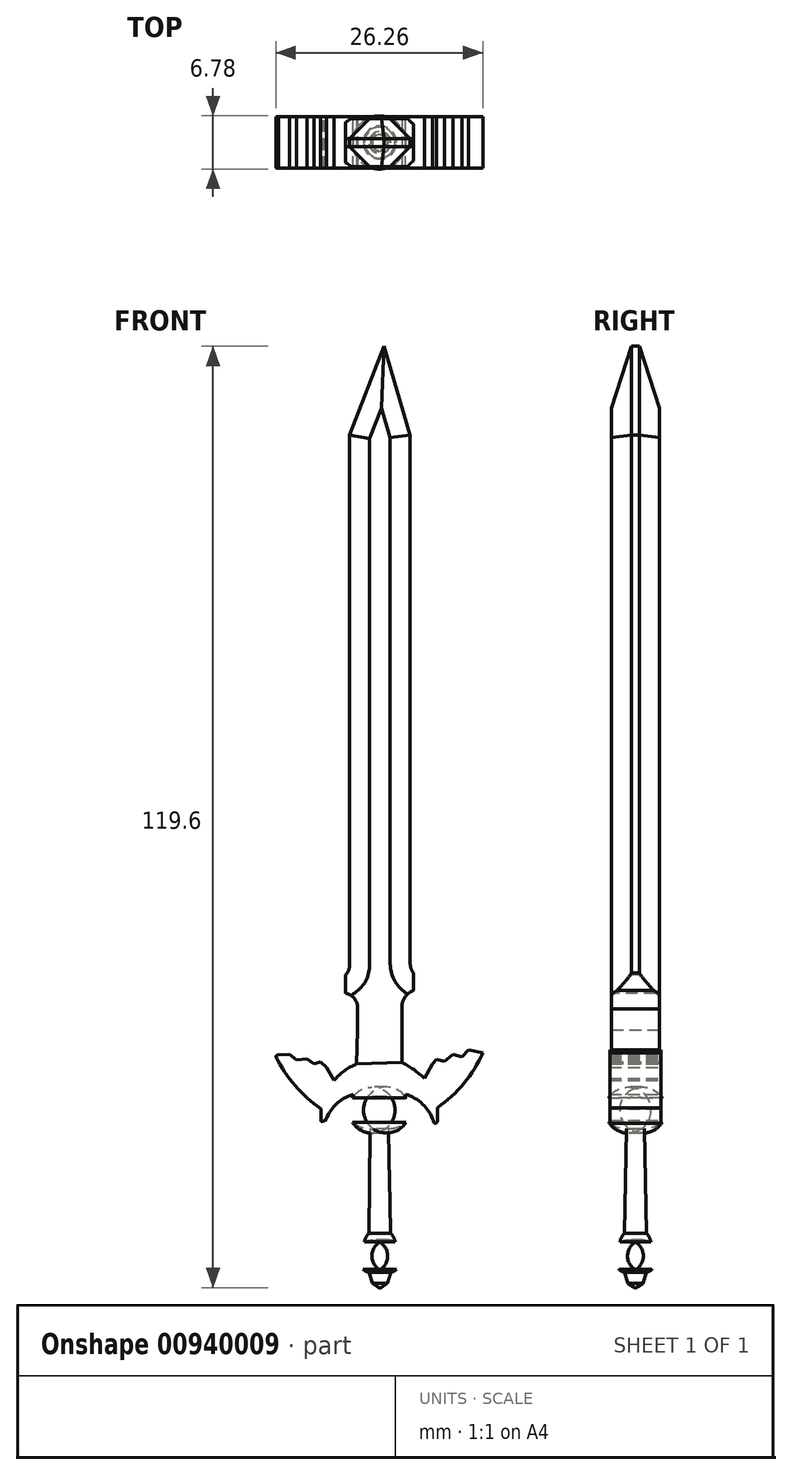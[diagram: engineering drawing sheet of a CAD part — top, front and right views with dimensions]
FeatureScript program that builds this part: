
annotation { "Feature Type Name" : "Feature", "Feature Type Description" : "" }
export const myFeature = defineFeature(function(context is Context, id is Id, definition is map)
    precondition{}
    {
        {
            var Q0;
            Q0=qCreatedBy(makeId("Front.planeOp"),FACE);
            var sketch = newSketch(context, id + "F0", { "sketchPlane" : qUnion([Q0])});
            skLineSegment(sketch, "E0", {"start": v(-4.41, -18.46) * mm, "end": v(-4.41, 49) * mm});
            skLineSegment(sketch, "E1", {"start": v(-4.41, 49) * mm, "end": v(0, 60.26) * mm});
            skLineSegment(sketch, "E2", {"start": v(0, 60.26) * mm, "end": v(3.3, 49) * mm});
            skLineSegment(sketch, "E3", {"start": v(3.3, 49) * mm, "end": v(3.3, -18.19) * mm});
            skArc(sketch, "E4", {"start": v(3.3, -18.19) * mm, "mid": v(3.41, -18.8) * mm, "end": v(3.72, -19.36) * mm});
            skLineSegment(sketch, "E5", {"start": v(3.72, -19.36) * mm, "end": v(3.72, -21.6) * mm});
            skArc(sketch, "E6", {"start": v(3.72, -21.6) * mm, "mid": v(2.57, -22.5) * mm, "end": v(2.26, -23.94) * mm});
            skArc(sketch, "E7", {"start": v(-4.9, -19.6) * mm, "mid": v(-4.54, -19.08) * mm, "end": v(-4.41, -18.46) * mm});
            skLineSegment(sketch, "E8", {"start": v(-4.9, -19.6) * mm, "end": v(-4.9, -21.94) * mm});
            skArc(sketch, "E9", {"start": v(-3.4, -23.94) * mm, "mid": v(-3.74, -22.63) * mm, "end": v(-4.9, -21.94) * mm});
            skLineSegment(sketch, "E10", {"start": v(-3.4, -23.94) * mm, "end": v(-3.4, -26.65) * mm});
            skLineSegment(sketch, "E11", {"start": v(2.26, -23.94) * mm, "end": v(2.26, -26.72) * mm});
            skLineSegment(sketch, "E12", {"start": v(2.26, -26.72) * mm, "end": v(2.28, -30.73) * mm});
            skArc(sketch, "E13", {"start": v(5.1, -32.73) * mm, "mid": v(3.76, -31.63) * mm, "end": v(2.28, -30.73) * mm});
            skLineSegment(sketch, "E14", {"start": v(5.1, -32.73) * mm, "end": v(6.16, -30.9) * mm});
            skLineSegment(sketch, "E15", {"start": v(6.16, -30.9) * mm, "end": v(6.67, -30.32) * mm});
            skLineSegment(sketch, "E16", {"start": v(6.67, -30.32) * mm, "end": v(7.65, -30.56) * mm});
            skLineSegment(sketch, "E17", {"start": v(7.65, -30.56) * mm, "end": v(8.74, -29.67) * mm});
            skLineSegment(sketch, "E18", {"start": v(8.74, -29.67) * mm, "end": v(9.9, -30.02) * mm});
            skLineSegment(sketch, "E19", {"start": v(9.9, -30.02) * mm, "end": v(10.74, -29.1) * mm});
            skLineSegment(sketch, "E20", {"start": v(10.74, -29.1) * mm, "end": v(12.53, -29.5) * mm});
            skArc(sketch, "E21", {"start": v(6.77, -36.46) * mm, "mid": v(10.13, -33.38) * mm, "end": v(12.53, -29.5) * mm});
            skLineSegment(sketch, "E22", {"start": v(6.77, -36.46) * mm, "end": v(6.77, -38.17) * mm});
            skArc(sketch, "E23", {"start": v(6.25, -38.17) * mm, "mid": v(6.51, -38.43) * mm, "end": v(6.77, -38.17) * mm});
            skArc(sketch, "E24", {"start": v(-8.05, -38.05) * mm, "mid": v(-7.96, -38.22) * mm, "end": v(-7.78, -38.17) * mm});
            skLineSegment(sketch, "E25", {"start": v(-8.05, -38.05) * mm, "end": v(-8.05, -36.59) * mm});
            skArc(sketch, "E26", {"start": v(-13.73, -30) * mm, "mid": v(-11.32, -33.67) * mm, "end": v(-8.05, -36.59) * mm});
            skArc(sketch, "E27", {"start": v(-13.45, -29.79) * mm, "mid": v(-13.64, -29.83) * mm, "end": v(-13.73, -30) * mm});
            skLineSegment(sketch, "E28", {"start": v(-13.45, -29.79) * mm, "end": v(-12.03, -29.7) * mm});
            skLineSegment(sketch, "E29", {"start": v(-12.03, -29.7) * mm, "end": v(-11.11, -30.37) * mm});
            skLineSegment(sketch, "E30", {"start": v(-11.11, -30.37) * mm, "end": v(-9.82, -30.24) * mm});
            skLineSegment(sketch, "E31", {"start": v(-9.82, -30.24) * mm, "end": v(-8.94, -30.88) * mm});
            skLineSegment(sketch, "E32", {"start": v(-8.94, -30.88) * mm, "end": v(-8.08, -30.65) * mm});
            skLineSegment(sketch, "E33", {"start": v(-8.08, -30.65) * mm, "end": v(-7.3, -31.32) * mm});
            skLineSegment(sketch, "E34", {"start": v(-7.3, -31.32) * mm, "end": v(-6.38, -33.01) * mm});
            skLineSegment(sketch, "E35", {"start": v(-3.4, -26.65) * mm, "end": v(-3.5, -30.93) * mm});
            skArc(sketch, "E36", {"start": v(-3.5, -30.93) * mm, "mid": v(-5.06, -31.8) * mm, "end": v(-6.38, -33.01) * mm});
            skArc(sketch, "E37", {"start": v(3.41, -37.88) * mm, "mid": v(3.4, -36.45) * mm, "end": v(2.7, -35.2) * mm});
            skArc(sketch, "E38", {"start": v(1.2, -39.14) * mm, "mid": v(2.34, -38.58) * mm, "end": v(3.41, -37.88) * mm});
            skArc(sketch, "E39", {"start": v(-4, -38.36) * mm, "mid": v(-2.95, -38.94) * mm, "end": v(-1.76, -39.14) * mm});
            skArc(sketch, "E40", {"start": v(-4, -35.2) * mm, "mid": v(-4.47, -36.78) * mm, "end": v(-4, -38.36) * mm});
            skLineSegment(sketch, "E41", {"start": v(-1.76, -39.14) * mm, "end": v(-1.95, -52.43) * mm});
            skLineSegment(sketch, "E42", {"start": v(1.2, -39.14) * mm, "end": v(1.2, -52.43) * mm});
            skArc(sketch, "E43", {"start": v(1.72, -53.51) * mm, "mid": v(1.63, -52.89) * mm, "end": v(1.2, -52.43) * mm});
            skArc(sketch, "E44", {"start": v(1.72, -57.03) * mm, "mid": v(2.81, -55.27) * mm, "end": v(1.72, -53.51) * mm});
            skArc(sketch, "E45", {"start": v(1.2, -57.15) * mm, "mid": v(1.46, -57.11) * mm, "end": v(1.72, -57.03) * mm});
            skArc(sketch, "E46", {"start": v(-2.52, -53.51) * mm, "mid": v(-3.6, -55.23) * mm, "end": v(-2.67, -57.03) * mm});
            skArc(sketch, "E47", {"start": v(-2.67, -57.03) * mm, "mid": v(-2.33, -57.25) * mm, "end": v(-1.95, -57.4) * mm});
            skLineSegment(sketch, "E48", {"start": v(-1.95, -57.4) * mm, "end": v(-1.5, -58.76) * mm});
            skLineSegment(sketch, "E49", {"start": v(-1.5, -58.76) * mm, "end": v(-0.82, -59.25) * mm});
            skArc(sketch, "E50", {"start": v(-0.82, -59.25) * mm, "mid": v(-0.54, -59.34) * mm, "end": v(-0.26, -59.25) * mm});
            skLineSegment(sketch, "E51", {"start": v(-0.26, -59.25) * mm, "end": v(0.55, -58.83) * mm});
            skLineSegment(sketch, "E52", {"start": v(0.55, -58.83) * mm, "end": v(1.2, -57.15) * mm});
            skArc(sketch, "E53", {"start": v(-1.95, -52.43) * mm, "mid": v(-2.31, -52.93) * mm, "end": v(-2.52, -53.51) * mm});
            skLineSegment(sketch, "E54", {"start": v(-0.63, -21.55) * mm, "end": v(-0.63, -21.55) * mm});
            skLineSegment(sketch, "E55", {"start": v(-1.95, -52.43) * mm, "end": v(1.2, -52.43) * mm});
            skPoint(sketch, "E56.0.midPoint", {"position": v(-0.63, -21.55) * mm});
            skLineSegment(sketch, "E57", {"start": v(-3.5, -30.93) * mm, "end": v(2.28, -30.73) * mm});
            skLineSegment(sketch, "E58", {"start": v(-0.63, -34.53) * mm, "end": v(-0.54, -58.87) * mm});
            skLineSegment(sketch, "E59", {"start": v(-0.54, -58.87) * mm, "end": v(-0.54, -59.34) * mm});
            skPoint(sketch, "E60.orphan", {"position": v(0.17, -34.5) * mm});
            skPoint(sketch, "E61.orphan", {"position": v(-1.43, -34.57) * mm});
            skLineSegment(sketch, "E62", {"start": v(2.7, -35.2) * mm, "end": v(2.7, -34.76) * mm});
            skLineSegment(sketch, "E63.MirrorCS", {"start": v(-3.95, -35.23) * mm, "end": v(-3.96, -34.79) * mm});
            skLineSegment(sketch, "E64", {"start": v(-3.95, -35.23) * mm, "end": v(-4, -35.2) * mm});
            skArc(sketch, "E65", {"start": v(6.25, -38.17) * mm, "mid": v(4.9, -36.03) * mm, "end": v(2.7, -34.76) * mm});
            skArc(sketch, "E66.MirrorCS", {"start": v(-7.48, -38.22) * mm, "mid": v(-6.14, -36.07) * mm, "end": v(-3.96, -34.79) * mm});
            skLineSegment(sketch, "E67", {"start": v(-7.48, -38.22) * mm, "end": v(-7.78, -38.17) * mm});
            skLineSegment(sketch, "E68", {"start": v(2.7, -35.2) * mm, "end": v(-3.95, -35.23) * mm});
            skSolve(sketch);
        }
        {
            var Q0;
            Q0=makeQuery(id+"F0.imprint","IMPRINT",FACE,{"disambiguationData":[TD([[makeQuery(id+"F0.imprint","IMPRINT",EDGE,{"derivedFrom":sQuery(id+"F0.wireOp",EDGE,"E39")}),1.0]])]});
            var Q1;
            Q1=makeQuery(id+"F0.imprint","IMPRINT",FACE,{"disambiguationData":[TD([[makeQuery(id+"F0.imprint","IMPRINT",EDGE,{"derivedFrom":sQuery(id+"F0.wireOp",EDGE,"E46")}),1.0]])]});
            var Q2;
            Q2=sQuery(id+"F0.wireOp",EDGE,"E58");
            revolve(context, id + "F1", {"surfaceOperationType" : NewSurfaceOperationType.NEW, "entities" : qUnion([Q0, Q1]), "axis" : qUnion([Q2]), "revolveType" : RevolveType.FULL});
        }
        {
            var Q0;
            Q0=makeQuery(id+"F0.imprint","IMPRINT",FACE,{"disambiguationData":[TD([[makeQuery(id+"F0.imprint","IMPRINT",EDGE,{"derivedFrom":sQuery(id+"F0.wireOp",EDGE,"E13")}),1.0]])]});
            extrude(context, id + "F2", {"entities" : qUnion([Q0]), "operationType" : NewBodyOperationType.ADD, "endBound" : BoundingType.SYMMETRIC, "depth" : 6.5 * mm, "offsetDistance" : 25.4 * mm});
        }
        {
            var Q0;
            Q0=makeQuery(id+"F0.imprint","IMPRINT",FACE,{"disambiguationData":[TD([[makeQuery(id+"F0.imprint","IMPRINT",EDGE,{"derivedFrom":sQuery(id+"F0.wireOp",EDGE,"E0")}),-1.0]])]});
            extrude(context, id + "F3", {"entities" : qUnion([Q0]), "operationType" : NewBodyOperationType.ADD, "endBound" : BoundingType.SYMMETRIC, "oppositeDirection" : true, "depth" : 6.1 * mm, "offsetDistance" : 25.4 * mm});
        }
        {
            var Q0;
            Q0=makeQuery(id+"F3.opExtrude","CAP_EDGE",EDGE,{"disambiguationData":[OSD([sQuery(id+"F0.wireOp",EDGE,"E1")])],"isStart":false});
            var Q1;
            Q1=makeQuery(id+"F3.opExtrude","CAP_EDGE",EDGE,{"disambiguationData":[OSD([sQuery(id+"F0.wireOp",EDGE,"E1")])],"isStart":true});
            var Q2;
            Q2=makeQuery(id+"F3.opExtrude","CAP_EDGE",EDGE,{"disambiguationData":[OSD([sQuery(id+"F0.wireOp",EDGE,"E0")])],"isStart":true});
            var Q3;
            Q3=makeQuery(id+"F3.opExtrude","CAP_EDGE",EDGE,{"disambiguationData":[OSD([sQuery(id+"F0.wireOp",EDGE,"E0")])],"isStart":false});
            var Q4;
            Q4=makeQuery(id+"F3.opExtrude","CAP_EDGE",EDGE,{"disambiguationData":[OSD([sQuery(id+"F0.wireOp",EDGE,"E2")])],"isStart":false});
            var Q5;
            Q5=makeQuery(id+"F3.opExtrude","CAP_EDGE",EDGE,{"disambiguationData":[OSD([sQuery(id+"F0.wireOp",EDGE,"E3")])],"isStart":false});
            var Q6;
            Q6=makeQuery(id+"F3.opExtrude","CAP_EDGE",EDGE,{"disambiguationData":[OSD([sQuery(id+"F0.wireOp",EDGE,"E3")])],"isStart":true});
            var Q7;
            Q7=makeQuery(id+"F3.opExtrude","CAP_EDGE",EDGE,{"disambiguationData":[OSD([sQuery(id+"F0.wireOp",EDGE,"E2")])],"isStart":true});
            chamfer(context, id + "F4", {"entities" : qUnion([Q0, Q1, Q2, Q3, Q4, Q5, Q6, Q7]), "width" : 2.54 * mm, "tangentPropagation" : true});
        }
    });
